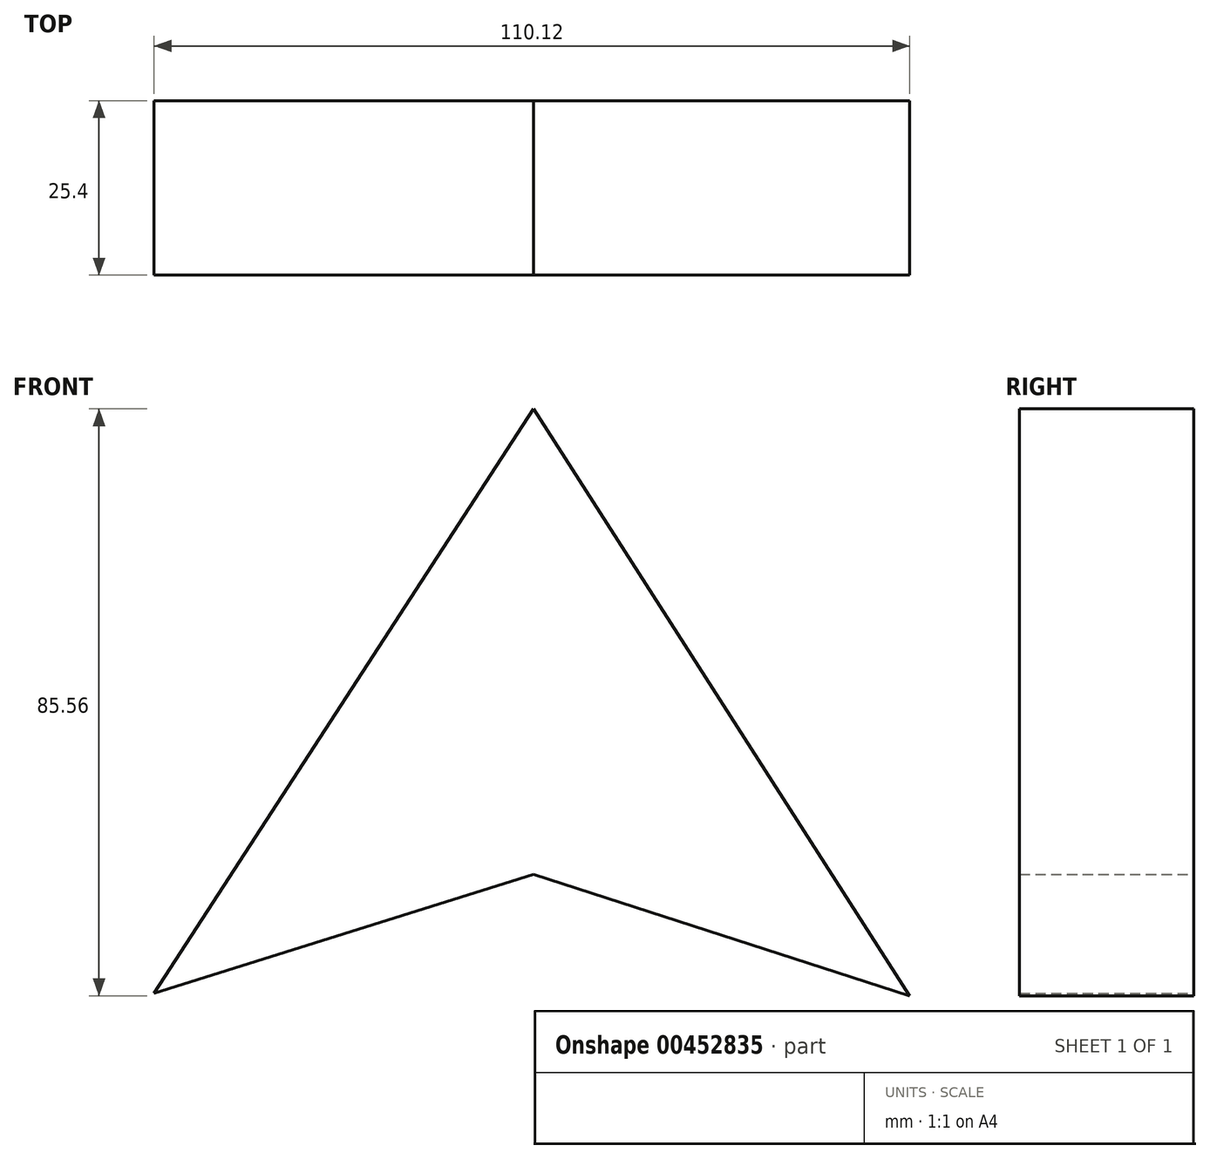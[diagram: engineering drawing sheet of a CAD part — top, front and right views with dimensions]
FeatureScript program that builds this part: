
annotation { "Feature Type Name" : "Feature", "Feature Type Description" : "" }
export const myFeature = defineFeature(function(context is Context, id is Id, definition is map)
    precondition{}
    {
        {
            var Q0;
            Q0=qCreatedBy(makeId("Front.planeOp"),FACE);
            var sketch = newSketch(context, id + "F0", { "sketchPlane" : qUnion([Q0])});
            skLineSegment(sketch, "E0", {"start": v(0, 67.89) * mm, "end": v(-55.32, -17.34) * mm});
            skLineSegment(sketch, "E1", {"start": v(0, 67.89) * mm, "end": v(54.8, -17.67) * mm});
            skLineSegment(sketch, "E2", {"start": v(54.8, -17.67) * mm, "end": v(0, 0) * mm});
            skLineSegment(sketch, "E3", {"start": v(0, 0) * mm, "end": v(-55.32, -17.34) * mm});
            skSolve(sketch);
        }
        {
            var Q0;
            Q0=makeQuery(id+"F0.imprint","IMPRINT",FACE,{"disambiguationData":[TD([[makeQuery(id+"F0.imprint","IMPRINT",EDGE,{"derivedFrom":sQuery(id+"F0.wireOp",EDGE,"E0")}),1.0]])]});
            extrude(context, id + "F1", {"entities" : qUnion([Q0]), "depth" : 25.4 * mm});
        }
    });
